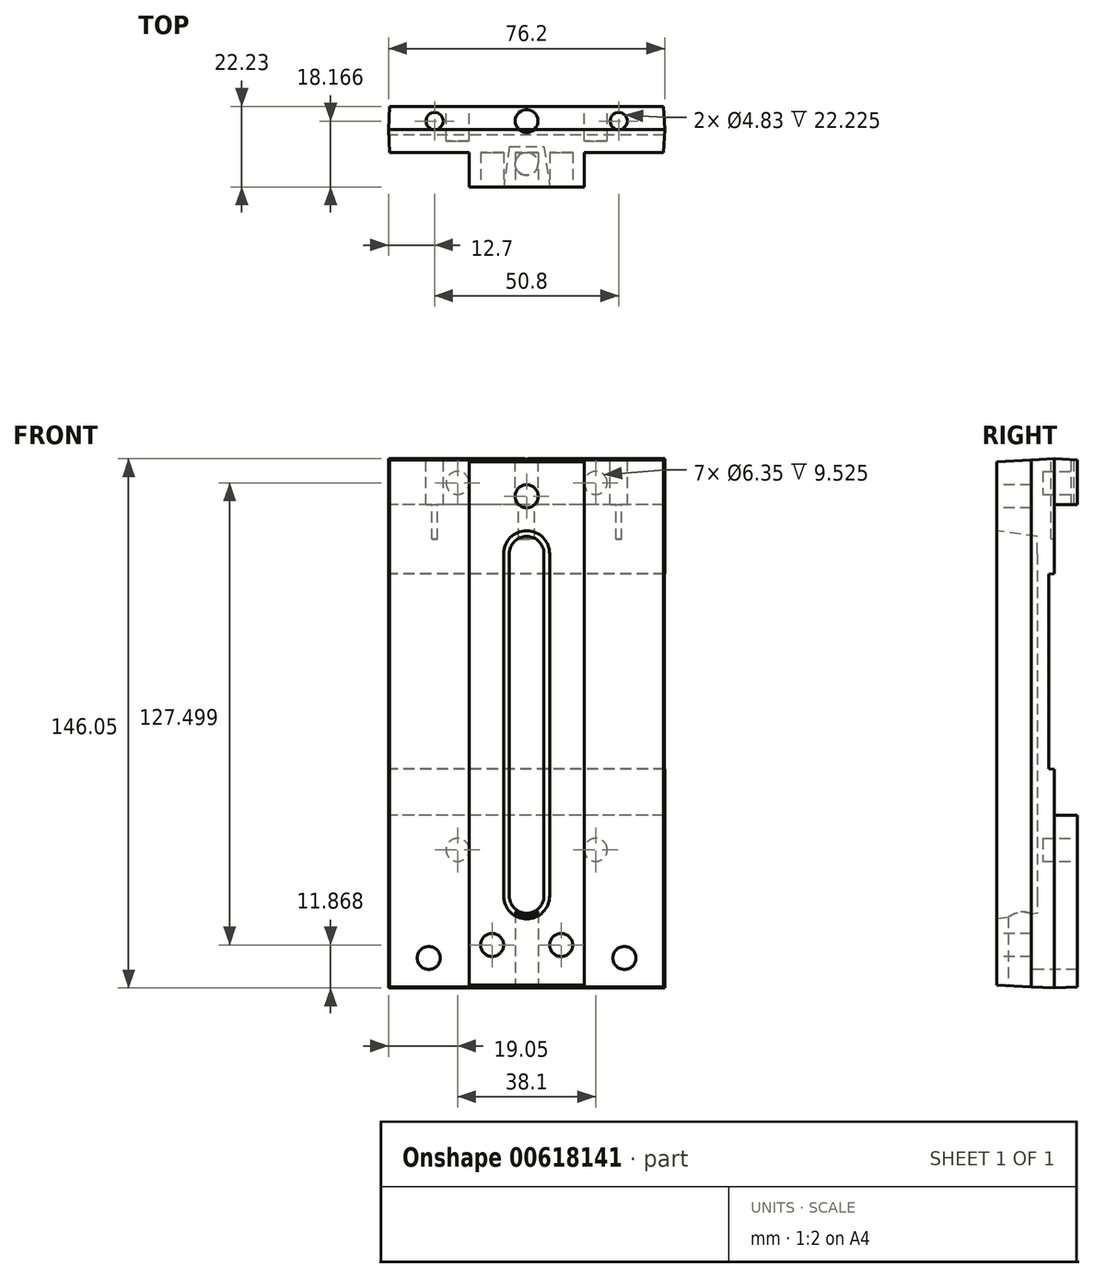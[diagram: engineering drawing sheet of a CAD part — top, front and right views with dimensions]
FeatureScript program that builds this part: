
annotation { "Feature Type Name" : "Feature", "Feature Type Description" : "" }
export const myFeature = defineFeature(function(context is Context, id is Id, definition is map)
    precondition{}
    {
        {
            var Q0;
            Q0=qCreatedBy(makeId("Front.planeOp"),FACE);
            var sketch = newSketch(context, id + "F0", { "sketchPlane" : qUnion([Q0])});
            skLineSegment(sketch, "E0.bottom", {"start": v(0, 0) * mm, "end": v(76.2, 0) * mm});
            skLineSegment(sketch, "E0.top", {"start": v(0, 146.05) * mm, "end": v(76.2, 146.05) * mm});
            skLineSegment(sketch, "E0.left", {"start": v(0, 0) * mm, "end": v(0, 146.05) * mm});
            skLineSegment(sketch, "E0.right", {"start": v(76.2, 0) * mm, "end": v(76.2, 146.05) * mm});
            skSolve(sketch);
        }
        {
            var Q0;
            Q0=qSketchRegion(id+"F0",true);
            extrude(context, id + "F1", {"entities" : qUnion([Q0]), "depth" : 15.88 * mm, "hasDraft" : true, "draftAngle" : 3 * degree, "draftPullDirection" : true, "hasSecondDirection" : true, "secondDirectionOppositeDirection" : true, "secondDirectionDepth" : 6.35 * mm, "hasSecondDirectionDraft" : true, "secondDirectionDraftAngle" : 3 * degree, "secondDirectionDraftPullDirection" : true});
        }
        {
            var Q0;
            Q0=qCreatedBy(makeId("Top.planeOp"),FACE);
            var sketch = newSketch(context, id + "F2", { "sketchPlane" : qUnion([Q0])});
            skLineSegment(sketch, "E1.0.0", {"start": v(0.83, -15.87) * mm, "end": v(0, 0) * mm});
            skLineSegment(sketch, "E1.0.1", {"start": v(0, 0) * mm, "end": v(76.2, 0) * mm});
            skLineSegment(sketch, "E1.0.2", {"start": v(76.2, 0) * mm, "end": v(75.37, -15.87) * mm});
            skLineSegment(sketch, "E1.0.3", {"start": v(0.83, -15.88) * mm, "end": v(75.37, -15.88) * mm});
            skLineSegment(sketch, "E2.bottom", {"start": v(22.22, -6.35) * mm, "end": v(-20.56, -6.35) * mm});
            skLineSegment(sketch, "E2.top", {"start": v(22.22, -25.4) * mm, "end": v(-20.56, -25.4) * mm});
            skLineSegment(sketch, "E2.left", {"start": v(22.22, -6.35) * mm, "end": v(22.22, -25.4) * mm});
            skLineSegment(sketch, "E2.right", {"start": v(-20.56, -6.35) * mm, "end": v(-20.56, -25.4) * mm});
            skPoint(sketch, "E2.middle", {"position": v(0.83, -15.87) * mm});
            skLineSegment(sketch, "E3.bottom", {"start": v(53.98, -6.35) * mm, "end": v(96.76, -6.35) * mm});
            skLineSegment(sketch, "E3.top", {"start": v(53.98, -25.4) * mm, "end": v(96.76, -25.4) * mm});
            skLineSegment(sketch, "E3.left", {"start": v(53.98, -6.35) * mm, "end": v(53.98, -25.4) * mm});
            skLineSegment(sketch, "E3.right", {"start": v(96.76, -6.35) * mm, "end": v(96.76, -25.4) * mm});
            skPoint(sketch, "E3.middle", {"position": v(75.37, -15.87) * mm});
            skSolve(sketch);
        }
        {
            var Q0;
            {var subQ0=sQuery(id+"F2.wireOp",EDGE,"E1.0.3");var subQ1=sQuery(id+"F2.wireOp",EDGE,"E1.0.0");var subQ2=makeQuery(id+"F2.imprint","INTERSECT",VERTEX,{"derivedFrom":[subQ1,subQ0]});Q0=makeQuery(id+"F2.imprint","IMPRINT",FACE,{"disambiguationData":[TD([[makeQuery(id+"F2.imprint","IMPRINT",EDGE,{"disambiguationData":[TD([[subQ2,-1.0]])],"derivedFrom":subQ1}),-1.0]])]});}
            var Q1;
            {var subQ0=sQuery(id+"F2.wireOp",EDGE,"E1.0.3");var subQ1=sQuery(id+"F2.wireOp",EDGE,"E1.0.2");var subQ2=makeQuery(id+"F2.imprint","INTERSECT",VERTEX,{"derivedFrom":[subQ1,subQ0]});Q1=makeQuery(id+"F2.imprint","IMPRINT",FACE,{"disambiguationData":[TD([[makeQuery(id+"F2.imprint","IMPRINT",EDGE,{"disambiguationData":[TD([[subQ2,1.0]])],"derivedFrom":subQ1}),-1.0]])]});}
            extrude(context, id + "F3", {"entities" : qUnion([Q0, Q1]), "operationType" : NewBodyOperationType.REMOVE, "endBound" : BoundingType.THROUGH_ALL, "depth" : 25.4 * mm});
        }
        {
            var Q0;
            Q0=qCreatedBy(makeId("Right.planeOp"),FACE);
            var sketch = newSketch(context, id + "F4", { "sketchPlane" : qUnion([Q0])});
            skLineSegment(sketch, "E4.0", {"start": v(6.35, 0.33) * mm, "end": v(6.35, 145.72) * mm});
            skLineSegment(sketch, "E5.0.0", {"start": v(-6.35, 145.72) * mm, "end": v(0, 146.05) * mm});
            skLineSegment(sketch, "E5.0.1", {"start": v(-6.35, 145.72) * mm, "end": v(-6.35, 0.33) * mm});
            skLineSegment(sketch, "E5.0.2", {"start": v(-6.35, 0.33) * mm, "end": v(0, 0) * mm});
            skLineSegment(sketch, "E5.0.3", {"start": v(0, 0) * mm, "end": v(0, 146.05) * mm});
            skLineSegment(sketch, "E6", {"start": v(6.35, 133.35) * mm, "end": v(0, 133.35) * mm});
            skLineSegment(sketch, "E7", {"start": v(0, 133.35) * mm, "end": v(0, 114.3) * mm});
            skLineSegment(sketch, "E8", {"start": v(0, 114.3) * mm, "end": v(-1.59, 114.22) * mm});
            skLineSegment(sketch, "E9", {"start": v(-1.59, 114.22) * mm, "end": v(-1.59, 60.4) * mm});
            skLineSegment(sketch, "E10", {"start": v(-1.59, 60.4) * mm, "end": v(0, 60.33) * mm});
            skLineSegment(sketch, "E11", {"start": v(0, 60.33) * mm, "end": v(0, 47.63) * mm});
            skLineSegment(sketch, "E12", {"start": v(0, 47.63) * mm, "end": v(6.35, 47.63) * mm});
            skSolve(sketch);
        }
        {
            var Q0;
            {var subQ1=sQuery(id+"F4.wireOp",EDGE,"E6");Q0=makeQuery(id+"F4.imprint","IMPRINT",FACE,{"disambiguationData":[TD([[makeQuery(id+"F4.imprint","IMPRINT",EDGE,{"derivedFrom":subQ1}),1.0]])]});}
            var Q1;
            {var subQ0=sQuery(id+"F4.wireOp",EDGE,"E8");Q1=makeQuery(id+"F4.imprint","IMPRINT",FACE,{"disambiguationData":[TD([[makeQuery(id+"F4.imprint","IMPRINT",EDGE,{"derivedFrom":subQ0}),1.0]])]});}
            extrude(context, id + "F5", {"entities" : qUnion([Q0, Q1]), "operationType" : NewBodyOperationType.REMOVE, "endBound" : BoundingType.THROUGH_ALL, "depth" : 25.4 * mm});
        }
        {
            var Q0;
            Q0=makeQuery(id+"F1.opExtrude","CAP_FACE",FACE,{"disambiguationData":[OSD([sQuery(id+"F0.wireOp",EDGE,"E0.bottom"),sQuery(id+"F0.wireOp",EDGE,"E0.top"),sQuery(id+"F0.wireOp",EDGE,"E0.left"),sQuery(id+"F0.wireOp",EDGE,"E0.right")])],"isStart":false});
            var sketch = newSketch(context, id + "F6", { "sketchPlane" : qUnion([Q0])});
            skLineSegment(sketch, "E13", {"start": v(38.1, 145.22) * mm, "end": v(38.1, 0) * mm, "construction": true});
            skLineSegment(sketch, "E14.bottom", {"start": v(44.45, 25.4) * mm, "end": v(31.75, 25.4) * mm});
            skLineSegment(sketch, "E14.top", {"start": v(44.45, 119.82) * mm, "end": v(31.75, 119.82) * mm});
            skLineSegment(sketch, "E14.left", {"start": v(44.45, 25.4) * mm, "end": v(44.45, 119.82) * mm});
            skLineSegment(sketch, "E14.right", {"start": v(31.75, 25.4) * mm, "end": v(31.75, 119.82) * mm});
            skPoint(sketch, "E14.middle", {"position": v(38.1, 72.6) * mm});
            skCircle(sketch, "E15", {"center": v(38.1, 119.82) * mm, "radius": 6.35 * mm});
            skCircle(sketch, "E16", {"center": v(38.1, 25.4) * mm, "radius": 6.35 * mm});
            skSolve(sketch);
        }
        {
            var Q0;
            Q0=qSketchRegion(id+"F6",true);
            extrude(context, id + "F7", {"entities" : qUnion([Q0]), "operationType" : NewBodyOperationType.REMOVE, "oppositeDirection" : true, "depth" : 11.1 * mm, "hasDraft" : true, "draftAngle" : 8 * degree, "draftPullDirection" : true});
        }
        {
            var Q0;
            Q0=makeQuery(id+"F1.opExtrude","CAP_FACE",FACE,{"disambiguationData":[OSD([sQuery(id+"F0.wireOp",EDGE,"E0.bottom"),sQuery(id+"F0.wireOp",EDGE,"E0.top"),sQuery(id+"F0.wireOp",EDGE,"E0.left"),sQuery(id+"F0.wireOp",EDGE,"E0.right")])],"isStart":false});
            var sketch = newSketch(context, id + "F8", { "sketchPlane" : qUnion([Q0])});
            skLineSegment(sketch, "E17", {"start": v(38.1, 145.22) * mm, "end": v(38.1, 0) * mm});
            skLineSegment(sketch, "E18", {"start": v(28.58, 11.87) * mm, "end": v(47.63, 11.87) * mm});
            skPoint(sketch, "E19", {"position": v(38.1, 11.87) * mm});
            skCircle(sketch, "E20", {"center": v(28.58, 11.87) * mm, "radius": 3.18 * mm});
            skCircle(sketch, "E21", {"center": v(47.63, 11.87) * mm, "radius": 3.18 * mm});
            skCircle(sketch, "E22", {"center": v(38.1, 135.7) * mm, "radius": 3.18 * mm});
            skSolve(sketch);
        }
        {
            var Q0;
            Q0=qSketchRegion(id+"F8",true);
            extrude(context, id + "F9", {"entities" : qUnion([Q0]), "operationType" : NewBodyOperationType.REMOVE, "oppositeDirection" : true, "depth" : 9.52 * mm});
        }
        {
            var Q0;
            {var subQ0=sQuery(id+"F0.wireOp",EDGE,"E0.top");var subQ1=sQuery(id+"F0.wireOp",EDGE,"E0.left");var subQ2=sQuery(id+"F0.wireOp",EDGE,"E0.right");Q0=makeQuery(id+"F5.boolean.opBoolean","SPLIT",FACE,{"disambiguationData":[TD([makeQuery(id+"F1.opExtrude","SWEPT_FACE",FACE,{"disambiguationData":[OSD([subQ0])]})])],"derivedFrom":makeQuery(id+"F1.opExtrude","CAP_FACE",FACE,{"disambiguationData":[OSD([sQuery(id+"F0.wireOp",EDGE,"E0.bottom"),subQ0,subQ1,subQ2])],"isStart":true})});}
            var sketch = newSketch(context, id + "F10", { "sketchPlane" : qUnion([Q0])});
            skLineSegment(sketch, "E23", {"start": v(-38.1, 145.72) * mm, "end": v(-38.1, 0) * mm});
            skLineSegment(sketch, "E24", {"start": v(-57.15, 139.37) * mm, "end": v(-19.05, 139.37) * mm});
            skLineSegment(sketch, "E25", {"start": v(-57.15, 38.1) * mm, "end": v(-19.05, 38.1) * mm});
            skPoint(sketch, "E26", {"position": v(-38.1, 139.37) * mm});
            skPoint(sketch, "E27", {"position": v(-38.1, 38.1) * mm});
            skCircle(sketch, "E28", {"center": v(-19.05, 139.37) * mm, "radius": 3.18 * mm});
            skCircle(sketch, "E29", {"center": v(-57.15, 139.37) * mm, "radius": 3.18 * mm});
            skCircle(sketch, "E30", {"center": v(-19.05, 38.1) * mm, "radius": 3.18 * mm});
            skCircle(sketch, "E31", {"center": v(-57.15, 38.1) * mm, "radius": 3.18 * mm});
            skSolve(sketch);
        }
        {
            var Q0;
            Q0=qSketchRegion(id+"F10",true);
            extrude(context, id + "F11", {"entities" : qUnion([Q0]), "operationType" : NewBodyOperationType.REMOVE, "oppositeDirection" : true, "depth" : 9.52 * mm});
        }
        {
            var Q0;
            {var subQ0=makeQuery(id+"F1.opExtrude","SWEPT_FACE",FACE,{"disambiguationData":[OSD([sQuery(id+"F0.wireOp",EDGE,"E0.right")])]});var subQ1=makeQuery(id+"F1.opExtrude","SWEPT_FACE",FACE,{"disambiguationData":[OSD([sQuery(id+"F0.wireOp",EDGE,"E0.top")])]});Q0=makeQuery(id+"F1.*.booleanUnion.opBoolean","MERGE",VERTEX,{"derivedFrom":[makeQuery(id+"F1.*.split.splitOp","SPLIT_SURFACE_INTERSECT",VERTEX,{"derivedFrom":[subQ1,subQ0]}),makeQuery(id+"F1.*.split.splitOp","SPLIT_SURFACE_INTERSECT",VERTEX,{"derivedFrom":[subQ1,subQ0],"isFromBackBody":true})]});}
            var Q1;
            Q1=qCreatedBy(makeId("Top.planeOp"),FACE);
            cPlane(context, id + "F12", {"entities" : qUnion([Q0, Q1]), "cplaneType" : CPlaneType.PLANE_POINT, "offset" : 25.4 * mm, "width" : 152.4 * mm, "height" : 152.4 * mm});
        }
        {
            var Q0;
            Q0=qCreatedBy(id+"F12.planeOp",FACE);
            var sketch = newSketch(context, id + "F13", { "sketchPlane" : qUnion([Q0])});
            skCircle(sketch, "E32", {"center": v(12.7, 2.29) * mm, "radius": 2.41 * mm});
            skCircle(sketch, "E33", {"center": v(63.5, 2.29) * mm, "radius": 2.41 * mm});
            skLineSegment(sketch, "E34.0.0", {"start": v(0.33, 6.35) * mm, "end": v(0, 0) * mm});
            skLineSegment(sketch, "E34.0.1", {"start": v(0, 0) * mm, "end": v(76.2, 0) * mm});
            skLineSegment(sketch, "E34.0.2", {"start": v(76.2, 0) * mm, "end": v(75.87, 6.35) * mm});
            skLineSegment(sketch, "E34.0.3", {"start": v(75.87, 6.35) * mm, "end": v(0.33, 6.35) * mm, "construction": true});
            skCircle(sketch, "E35", {"center": v(38.1, 2.29) * mm, "radius": 3.18 * mm});
            skLineSegment(sketch, "E36", {"start": v(38.1, 6.35) * mm, "end": v(38.1, 2.29) * mm, "construction": true});
            skSolve(sketch);
        }
        {
            var Q0;
            Q0=qSketchRegion(id+"F13",true);
            extrude(context, id + "F14", {"entities" : qUnion([Q0]), "operationType" : NewBodyOperationType.REMOVE, "oppositeDirection" : true, "depth" : 22.22 * mm});
        }
        {
            var Q0;
            Q0=qCreatedBy(makeId("Top.planeOp"),FACE);
            var sketch = newSketch(context, id + "F15", { "sketchPlane" : qUnion([Q0])});
            skCircle(sketch, "E37", {"center": v(38.1, -9.52) * mm, "radius": 3.18 * mm});
            skSolve(sketch);
        }
        {
            var Q0;
            Q0=qSketchRegion(id+"F15",true);
            extrude(context, id + "F16", {"entities" : qUnion([Q0]), "operationType" : NewBodyOperationType.REMOVE, "depth" : 25.4 * mm});
        }
        {
            var Q0;
            Q0=makeQuery(id+"F3.boolean.opBoolean","COPY",FACE,{"derivedFrom":makeQuery(id+"F3.opExtrude","SWEPT_FACE",FACE,{"disambiguationData":[OSD([sQuery(id+"F2.wireOp",EDGE,"E3.bottom")])]})});
            var sketch = newSketch(context, id + "F17", { "sketchPlane" : qUnion([Q0])});
            skLineSegment(sketch, "E38.0", {"start": v(22.22, 145.72) * mm, "end": v(22.22, 0.33) * mm});
            skLineSegment(sketch, "E39.0", {"start": v(0, 0) * mm, "end": v(0, 47.62) * mm});
            skLineSegment(sketch, "E40.0", {"start": v(53.98, 145.72) * mm, "end": v(53.98, 0.33) * mm});
            skLineSegment(sketch, "E41.0", {"start": v(76.2, 0) * mm, "end": v(76.2, 47.62) * mm});
            skLineSegment(sketch, "E42", {"start": v(53.98, 8.27) * mm, "end": v(76.2, 8.27) * mm});
            skLineSegment(sketch, "E43", {"start": v(0, 8.27) * mm, "end": v(22.22, 8.27) * mm});
            skCircle(sketch, "E44", {"center": v(11.11, 8.27) * mm, "radius": 3.18 * mm});
            skCircle(sketch, "E45", {"center": v(65.09, 8.27) * mm, "radius": 3.18 * mm});
            skSolve(sketch);
        }
        {
            var Q0;
            Q0=qSketchRegion(id+"F17",true);
            extrude(context, id + "F18", {"entities" : qUnion([Q0]), "operationType" : NewBodyOperationType.REMOVE, "endBound" : BoundingType.THROUGH_ALL, "oppositeDirection" : true, "depth" : 25.4 * mm});
        }
    });
